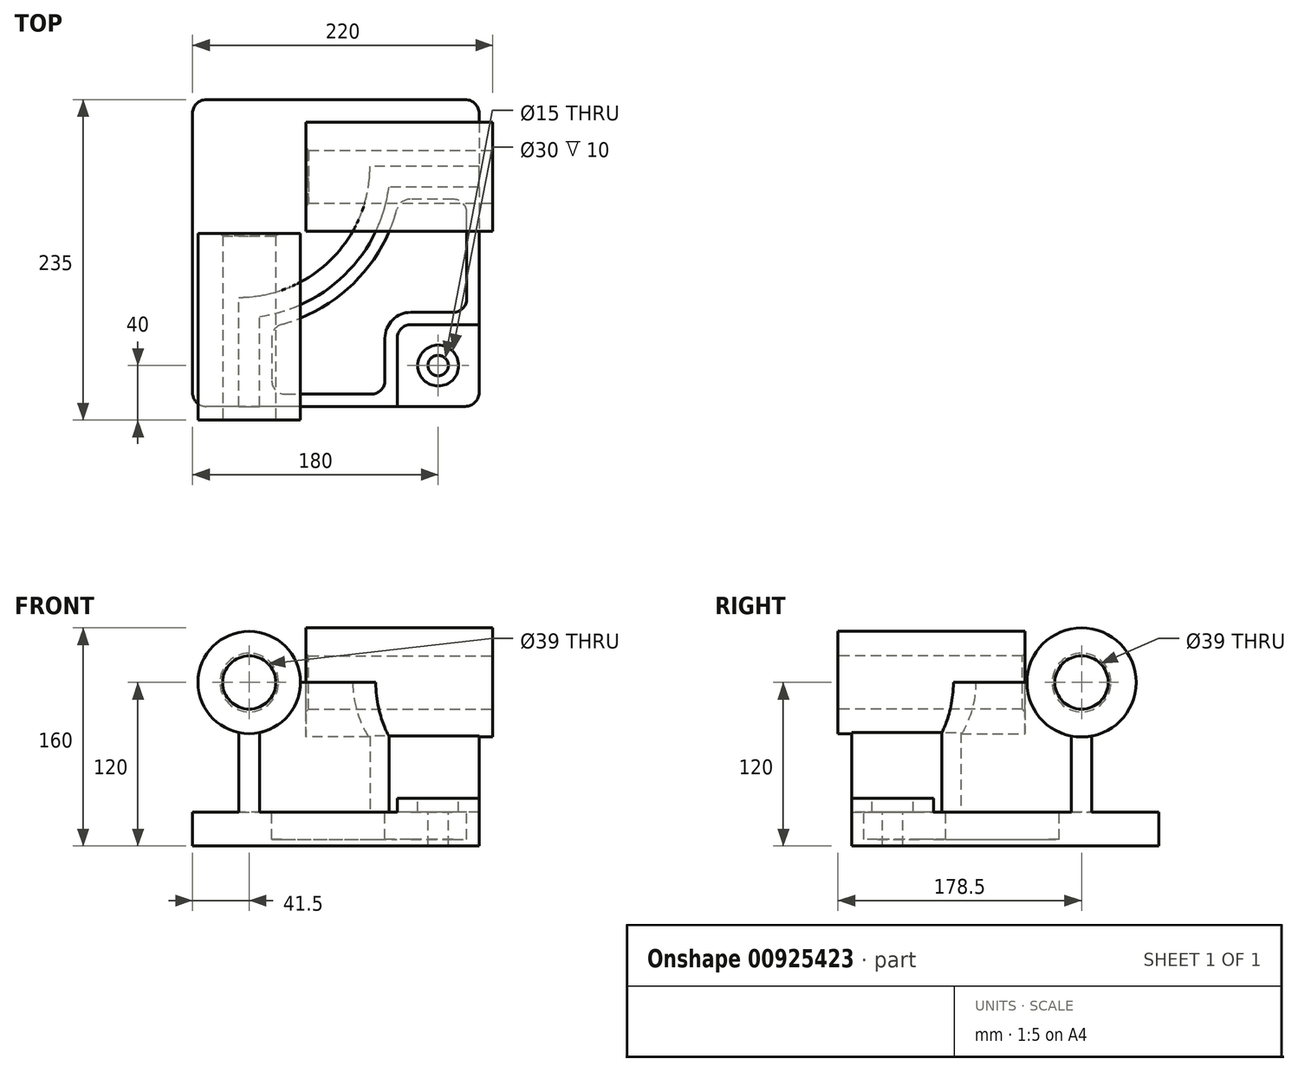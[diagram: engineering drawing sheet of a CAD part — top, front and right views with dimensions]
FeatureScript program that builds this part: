
annotation { "Feature Type Name" : "Feature", "Feature Type Description" : "" }
export const myFeature = defineFeature(function(context is Context, id is Id, definition is map)
    precondition{}
    {
        {
            var Q0;
            Q0=qCreatedBy(makeId("Top.planeOp"),FACE);
            var sketch = newSketch(context, id + "F0", { "sketchPlane" : qUnion([Q0])});
            skLineSegment(sketch, "E0.bottom", {"start": v(105, 112.5) * mm, "end": v(-105, 112.5) * mm});
            skLineSegment(sketch, "E0.top", {"start": v(105, -112.5) * mm, "end": v(-105, -112.5) * mm});
            skLineSegment(sketch, "E0.left", {"start": v(105, 112.5) * mm, "end": v(105, -112.5) * mm});
            skLineSegment(sketch, "E0.right", {"start": v(-105, 112.5) * mm, "end": v(-105, -112.5) * mm});
            skPoint(sketch, "E0.middle", {"position": v(0, 0) * mm});
            skSolve(sketch);
        }
        {
            var Q0;
            Q0=makeQuery(id+"F0.imprint","IMPRINT",FACE,{"disambiguationData":[TD([[makeQuery(id+"F0.imprint","IMPRINT",EDGE,{"derivedFrom":sQuery(id+"F0.wireOp",EDGE,"E0.bottom")}),1.0]])]});
            extrude(context, id + "F1", {"entities" : qUnion([Q0]), "depth" : 25 * mm, "offsetDistance" : 25.4 * mm});
        }
        {
            var Q0;
            Q0=makeQuery(id+"F1.opExtrude","CAP_FACE",FACE,{"disambiguationData":[OSD([sQuery(id+"F0.wireOp",EDGE,"E0.bottom"),sQuery(id+"F0.wireOp",EDGE,"E0.top"),sQuery(id+"F0.wireOp",EDGE,"E0.left"),sQuery(id+"F0.wireOp",EDGE,"E0.right")])],"isStart":false});
            var sketch = newSketch(context, id + "F2", { "sketchPlane" : qUnion([Q0])});
            skLineSegment(sketch, "E1", {"start": v(-71, -112.5) * mm, "end": v(-71, -32.5) * mm});
            skLineSegment(sketch, "E2", {"start": v(105, 63.5) * mm, "end": v(25, 63.5) * mm});
            skArc(sketch, "E3", {"start": v(-71, -32.5) * mm, "mid": v(-3.12, -4.38) * mm, "end": v(25, 63.5) * mm});
            skLineSegment(sketch, "E4", {"start": v(-71, 63.5) * mm, "end": v(25, 63.5) * mm, "construction": true});
            skLineSegment(sketch, "E5", {"start": v(-71, 63.5) * mm, "end": v(-71, -32.5) * mm, "construction": true});
            skLineSegment(sketch, "E6.0", {"start": v(-56, -112.5) * mm, "end": v(-56, -46.48) * mm});
            skArc(sketch, "E6.1", {"start": v(-56, -46.48) * mm, "mid": v(7.49, -14.99) * mm, "end": v(38.98, 48.5) * mm});
            skLineSegment(sketch, "E6.2", {"start": v(105, 48.5) * mm, "end": v(38.98, 48.5) * mm});
            skLineSegment(sketch, "E7.0", {"start": v(105, 112.5) * mm, "end": v(105, -112.5) * mm});
            skLineSegment(sketch, "E8.0", {"start": v(105, -112.5) * mm, "end": v(-105, -112.5) * mm});
            skSolve(sketch);
        }
        {
            var Q0;
            {var subQ2=sQuery(id+"F2.wireOp",EDGE,"E1");Q0=makeQuery(id+"F2.imprint","IMPRINT",FACE,{"disambiguationData":[TD([[makeQuery(id+"F2.imprint","IMPRINT",EDGE,{"derivedFrom":subQ2}),-1.0]])]});}
            extrude(context, id + "F3", {"entities" : qUnion([Q0]), "operationType" : NewBodyOperationType.ADD, "depth" : 95 * mm, "offsetDistance" : 25.4 * mm});
        }
        {
            var Q0;
            Q0=makeQuery(id+"F3.boolean.opBoolean","MERGE",FACE,{"derivedFrom":[makeQuery(id+"F1.opExtrude","SWEPT_FACE",FACE,{"disambiguationData":[OSD([sQuery(id+"F0.wireOp",EDGE,"E0.top")])]}),makeQuery(id+"F3.opExtrude","SWEPT_FACE",FACE,{"disambiguationData":[OSD([sQuery(id+"F2.wireOp",EDGE,"E8.0")])]})]});
            var sketch = newSketch(context, id + "F4", { "sketchPlane" : qUnion([Q0])});
            skCircle(sketch, "E9", {"center": v(-63.5, 120) * mm, "radius": 37.5 * mm});
            skSolve(sketch);
        }
        {
            var Q0;
            Q0 = qSketchRegion(id + "F4", true);
            extrude(context, id + "F5", {"entities" : qUnion([Q0]), "operationType" : NewBodyOperationType.ADD, "depth" : 10 * mm, "offsetDistance" : 25.4 * mm, "hasSecondDirection" : true, "secondDirectionOppositeDirection" : true, "secondDirectionDepth" : 127 * mm});
        }
        {
            var Q0;
            Q0=makeQuery(id+"F3.boolean.opBoolean","MERGE",FACE,{"derivedFrom":[makeQuery(id+"F1.opExtrude","SWEPT_FACE",FACE,{"disambiguationData":[OSD([sQuery(id+"F0.wireOp",EDGE,"E0.left")])]}),makeQuery(id+"F3.opExtrude","SWEPT_FACE",FACE,{"disambiguationData":[OSD([sQuery(id+"F2.wireOp",EDGE,"E7.0")])]})]});
            var sketch = newSketch(context, id + "F6", { "sketchPlane" : qUnion([Q0])});
            skCircle(sketch, "E10", {"center": v(56, 120) * mm, "radius": 40 * mm});
            skSolve(sketch);
        }
        {
            var Q0;
            Q0 = qSketchRegion(id + "F6", true);
            extrude(context, id + "F7", {"entities" : qUnion([Q0]), "operationType" : NewBodyOperationType.ADD, "depth" : 10 * mm, "offsetDistance" : 25.4 * mm, "hasSecondDirection" : true, "secondDirectionOppositeDirection" : true, "secondDirectionDepth" : 127 * mm});
        }
        {
            var Q0;
            {var subQ0=sQuery(id+"F0.wireOp",EDGE,"E0.left");var subQ1=sQuery(id+"F0.wireOp",EDGE,"E0.top");Q0=makeQuery(id+"F3.boolean.opBoolean","SPLIT",FACE,{"disambiguationData":[TD([makeQuery(id+"F3.opExtrude","SWEPT_FACE",FACE,{"disambiguationData":[OSD([sQuery(id+"F2.wireOp",EDGE,"E6.0")])]})])],"derivedFrom":makeQuery(id+"F1.opExtrude","CAP_FACE",FACE,{"disambiguationData":[OSD([sQuery(id+"F0.wireOp",EDGE,"E0.bottom"),subQ1,subQ0,sQuery(id+"F0.wireOp",EDGE,"E0.right")])],"isStart":false})});}
            var sketch = newSketch(context, id + "F8", { "sketchPlane" : qUnion([Q0])});
            skLineSegment(sketch, "E11.bottom", {"start": v(105, -112.5) * mm, "end": v(45, -112.5) * mm});
            skLineSegment(sketch, "E11.top", {"start": v(105, -52.5) * mm, "end": v(45, -52.5) * mm});
            skLineSegment(sketch, "E11.left", {"start": v(105, -112.5) * mm, "end": v(105, -52.5) * mm});
            skLineSegment(sketch, "E11.right", {"start": v(45, -112.5) * mm, "end": v(45, -52.5) * mm});
            skSolve(sketch);
        }
        {
            var Q0;
            Q0 = qSketchRegion(id + "F8", true);
            extrude(context, id + "F9", {"entities" : qUnion([Q0]), "operationType" : NewBodyOperationType.ADD, "depth" : 10 * mm, "offsetDistance" : 25.4 * mm});
        }
        {
            var Q0;
            Q0=makeQuery(id+"F9.opExtrude","SWEPT_EDGE",EDGE,{"disambiguationData":[OSD([sQuery(id+"F8.wireOp",EDGE,"E11.top"),sQuery(id+"F8.wireOp",EDGE,"E11.right")])]});
            fillet(context, id + "F10", {"entities" : qUnion([Q0]), "radius" : 10 * mm, "tangentPropagation" : true, "allowEdgeOverflow" : false});
        }
        {
            var Q0;
            {var subQ0=sQuery(id+"F0.wireOp",EDGE,"E0.left");var subQ1=sQuery(id+"F0.wireOp",EDGE,"E0.top");Q0=makeQuery(id+"F3.boolean.opBoolean","SPLIT",FACE,{"disambiguationData":[TD([makeQuery(id+"F3.opExtrude","SWEPT_FACE",FACE,{"disambiguationData":[OSD([sQuery(id+"F2.wireOp",EDGE,"E6.0")])]})])],"derivedFrom":makeQuery(id+"F1.opExtrude","CAP_FACE",FACE,{"disambiguationData":[OSD([sQuery(id+"F0.wireOp",EDGE,"E0.bottom"),subQ1,subQ0,sQuery(id+"F0.wireOp",EDGE,"E0.right")])],"isStart":false})});}
            var sketch = newSketch(context, id + "F11", { "sketchPlane" : qUnion([Q0])});
            skLineSegment(sketch, "E12.0", {"start": v(-47, -54.08) * mm, "end": v(-47, -103.5) * mm});
            skArc(sketch, "E12.1", {"start": v(46.58, 39.5) * mm, "mid": v(13.85, -21.35) * mm, "end": v(-47, -54.08) * mm});
            skLineSegment(sketch, "E12.2", {"start": v(-47, -103.5) * mm, "end": v(36, -103.5) * mm});
            skLineSegment(sketch, "E12.3", {"start": v(96, 39.5) * mm, "end": v(46.58, 39.5) * mm});
            skLineSegment(sketch, "E12.4", {"start": v(36, -103.5) * mm, "end": v(36, -62.5) * mm});
            skArc(sketch, "E12.5", {"start": v(36, -62.5) * mm, "mid": v(41.56, -49.06) * mm, "end": v(55, -43.5) * mm});
            skLineSegment(sketch, "E12.6", {"start": v(55, -43.5) * mm, "end": v(96, -43.5) * mm});
            skLineSegment(sketch, "E12.7", {"start": v(96, -43.5) * mm, "end": v(96, 39.5) * mm});
            skSolve(sketch);
        }
        {
            var Q0;
            Q0 = qSketchRegion(id + "F11", true);
            extrude(context, id + "F12", {"entities" : qUnion([Q0]), "operationType" : NewBodyOperationType.REMOVE, "oppositeDirection" : true, "depth" : 20 * mm, "offsetDistance" : 25.4 * mm});
        }
        {
            var Q0;
            Q0=makeQuery(id+"F9.opExtrude","CAP_FACE",FACE,{"disambiguationData":[OSD([sQuery(id+"F8.wireOp",EDGE,"E11.bottom"),sQuery(id+"F8.wireOp",EDGE,"E11.top"),sQuery(id+"F8.wireOp",EDGE,"E11.left"),sQuery(id+"F8.wireOp",EDGE,"E11.right")])],"isStart":false});
            var sketch = newSketch(context, id + "F13", { "sketchPlane" : qUnion([Q0])});
            skCircle(sketch, "E13", {"center": v(75, -82.5) * mm, "radius": 15 * mm});
            skSolve(sketch);
        }
        {
            var Q0;
            Q0=sQuery(id+"F13.wireOp",VERTEX,"E13.center");
            var Q1;
            Q1=makeQuery(id+"F1.opExtrude","SWEPT_BODY",BODY,{"disambiguationData":[OSD([sQuery(id+"F0.wireOp",EDGE,"E0.bottom"),sQuery(id+"F0.wireOp",EDGE,"E0.top"),sQuery(id+"F0.wireOp",EDGE,"E0.left"),sQuery(id+"F0.wireOp",EDGE,"E0.right")])]});
            hole(context, id + "F14", {"style" : HoleStyle.C_BORE, "endStyle" : HoleEndStyle.THROUGH, "holeDiameter" : 15 * mm, "cBoreDiameter" : 30 * mm, "cBoreDepth" : 10 * mm, "majorDiameter" : 6.35 * mm, "isTappedThrough" : true, "tappedDepth" : 12.7 * mm, "tapClearance" : 3, "locations" : qUnion([Q0]), "scope" : qUnion([Q1])});
        }
        {
            var Q0;
            Q0=makeQuery(id+"F12.boolean.opBoolean","COPY",EDGE,{"derivedFrom":makeQuery(id+"F12.opExtrude","SWEPT_EDGE",EDGE,{"disambiguationData":[OSD([sQuery(id+"F11.wireOp",EDGE,"E12.0"),sQuery(id+"F11.wireOp",EDGE,"E12.1")])]})});
            var Q1;
            Q1=makeQuery(id+"F12.boolean.opBoolean","COPY",EDGE,{"derivedFrom":makeQuery(id+"F12.opExtrude","SWEPT_EDGE",EDGE,{"disambiguationData":[OSD([sQuery(id+"F11.wireOp",EDGE,"E12.1"),sQuery(id+"F11.wireOp",EDGE,"E12.3")])]})});
            var Q2;
            Q2=makeQuery(id+"F12.boolean.opBoolean","COPY",EDGE,{"derivedFrom":makeQuery(id+"F12.opExtrude","SWEPT_EDGE",EDGE,{"disambiguationData":[OSD([sQuery(id+"F11.wireOp",EDGE,"E12.3"),sQuery(id+"F11.wireOp",EDGE,"E12.7")])]})});
            var Q3;
            Q3=makeQuery(id+"F12.boolean.opBoolean","COPY",EDGE,{"derivedFrom":makeQuery(id+"F12.opExtrude","SWEPT_EDGE",EDGE,{"disambiguationData":[OSD([sQuery(id+"F11.wireOp",EDGE,"E12.0"),sQuery(id+"F11.wireOp",EDGE,"E12.2")])]})});
            var Q4;
            Q4=makeQuery(id+"F12.boolean.opBoolean","COPY",EDGE,{"derivedFrom":makeQuery(id+"F12.opExtrude","SWEPT_EDGE",EDGE,{"disambiguationData":[OSD([sQuery(id+"F11.wireOp",EDGE,"E12.2"),sQuery(id+"F11.wireOp",EDGE,"E12.4")])]})});
            var Q5;
            Q5=makeQuery(id+"F12.boolean.opBoolean","COPY",EDGE,{"derivedFrom":makeQuery(id+"F12.opExtrude","SWEPT_EDGE",EDGE,{"disambiguationData":[OSD([sQuery(id+"F11.wireOp",EDGE,"E12.6"),sQuery(id+"F11.wireOp",EDGE,"E12.7")])]})});
            fillet(context, id + "F15", {"entities" : qUnion([Q0, Q1, Q2, Q3, Q4, Q5]), "radius" : 10 * mm, "tangentPropagation" : true, "allowEdgeOverflow" : false});
        }
        {
            var Q0;
            Q0=makeQuery(id+"F5.opExtrude","CAP_FACE",FACE,{"disambiguationData":[OSD([sQuery(id+"F4.wireOp",EDGE,"E9")])],"isStart":false});
            var sketch = newSketch(context, id + "F16", { "sketchPlane" : qUnion([Q0])});
            skCircle(sketch, "E14", {"center": v(-63.5, 120) * mm, "radius": 19.5 * mm});
            skSolve(sketch);
        }
        {
            var Q0;
            Q0 = qSketchRegion(id + "F16", true);
            extrude(context, id + "F17", {"entities" : qUnion([Q0]), "operationType" : NewBodyOperationType.REMOVE, "endBound" : BoundingType.THROUGH_ALL, "oppositeDirection" : true, "depth" : 25.4 * mm, "offsetDistance" : 25.4 * mm});
        }
        {
            var Q0;
            Q0=makeQuery(id+"F7.opExtrude","CAP_FACE",FACE,{"disambiguationData":[OSD([sQuery(id+"F6.wireOp",EDGE,"E10")])],"isStart":false});
            var sketch = newSketch(context, id + "F18", { "sketchPlane" : qUnion([Q0])});
            skCircle(sketch, "E15", {"center": v(56, 120) * mm, "radius": 19.5 * mm});
            skSolve(sketch);
        }
        {
            var Q0;
            Q0=makeQuery(id+"F18.imprint","IMPRINT",FACE,{"disambiguationData":[TD([[makeQuery(id+"F18.imprint","IMPRINT",EDGE,{"derivedFrom":sQuery(id+"F18.wireOp",EDGE,"E15")}),1.0]])]});
            extrude(context, id + "F19", {"entities" : qUnion([Q0]), "operationType" : NewBodyOperationType.REMOVE, "endBound" : BoundingType.THROUGH_ALL, "oppositeDirection" : true, "depth" : 25.4 * mm, "offsetDistance" : 25.4 * mm});
        }
        {
            var Q0;
            Q0=makeQuery(id+"F17.boolean.opBoolean","COPY",EDGE,{"derivedFrom":makeQuery(id+"F17.opExtrude","CAP_EDGE",EDGE,{"disambiguationData":[OSD([sQuery(id+"F16.wireOp",EDGE,"E14")])],"isStart":true})});
            var Q1;
            Q1=makeQuery(id+"F19.boolean.opBoolean","COPY",EDGE,{"derivedFrom":makeQuery(id+"F19.opExtrude","CAP_EDGE",EDGE,{"disambiguationData":[OSD([sQuery(id+"F18.wireOp",EDGE,"E15")])],"isStart":true})});
            var Q2;
            Q2=makeQuery(id+"F19.boolean.opBoolean","INTERSECT",EDGE,{"derivedFrom":[makeQuery(id+"F7.opExtrude","CAP_FACE",FACE,{"disambiguationData":[OSD([sQuery(id+"F6.wireOp",EDGE,"E10")])],"isStart":true}),makeQuery(id+"F19.opExtrude","SWEPT_FACE",FACE,{"disambiguationData":[OSD([sQuery(id+"F18.wireOp",EDGE,"E15")])]})]});
            var Q3;
            Q3=makeQuery(id+"F17.boolean.opBoolean","INTERSECT",EDGE,{"derivedFrom":[makeQuery(id+"F5.opExtrude","CAP_FACE",FACE,{"disambiguationData":[OSD([sQuery(id+"F4.wireOp",EDGE,"E9")])],"isStart":true}),makeQuery(id+"F17.opExtrude","SWEPT_FACE",FACE,{"disambiguationData":[OSD([sQuery(id+"F16.wireOp",EDGE,"E14")])]})]});
            chamfer(context, id + "F20", {"entities" : qUnion([Q0, Q1, Q2, Q3]), "width" : 2 * mm, "tangentPropagation" : true});
        }
        {
            var Q0;
            Q0=makeQuery(id+"F1.opExtrude","SWEPT_EDGE",EDGE,{"disambiguationData":[OSD([sQuery(id+"F0.wireOp",EDGE,"E0.top"),sQuery(id+"F0.wireOp",EDGE,"E0.right")])]});
            var Q1;
            Q1=makeQuery(id+"F9.boolean.opBoolean","MERGE",EDGE,{"derivedFrom":[makeQuery(id+"F1.opExtrude","SWEPT_EDGE",EDGE,{"disambiguationData":[OSD([sQuery(id+"F0.wireOp",EDGE,"E0.top"),sQuery(id+"F0.wireOp",EDGE,"E0.left")])]}),makeQuery(id+"F9.opExtrude","SWEPT_EDGE",EDGE,{"disambiguationData":[OSD([sQuery(id+"F8.wireOp",EDGE,"E11.bottom"),sQuery(id+"F8.wireOp",EDGE,"E11.left")])]})]});
            var Q2;
            Q2=makeQuery(id+"F1.opExtrude","SWEPT_EDGE",EDGE,{"disambiguationData":[OSD([sQuery(id+"F0.wireOp",EDGE,"E0.bottom"),sQuery(id+"F0.wireOp",EDGE,"E0.left")])]});
            var Q3;
            Q3=makeQuery(id+"F1.opExtrude","SWEPT_EDGE",EDGE,{"disambiguationData":[OSD([sQuery(id+"F0.wireOp",EDGE,"E0.bottom"),sQuery(id+"F0.wireOp",EDGE,"E0.right")])]});
            fillet(context, id + "F21", {"entities" : qUnion([Q0, Q1, Q2, Q3]), "radius" : 10 * mm, "tangentPropagation" : true, "allowEdgeOverflow" : false});
        }
    });
